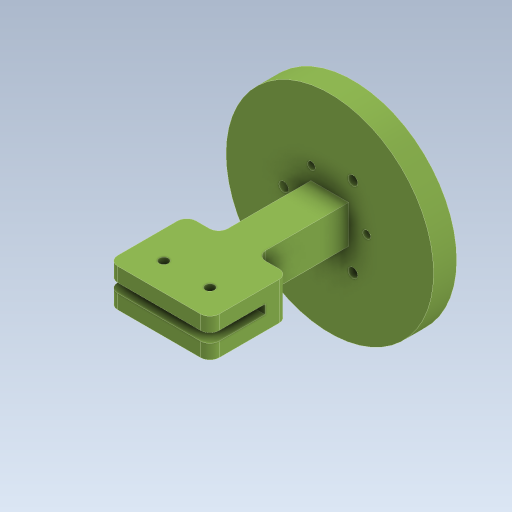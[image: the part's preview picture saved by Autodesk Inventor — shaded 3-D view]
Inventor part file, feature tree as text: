
AUTODESK INVENTOR PART (.ipt)
format: ipt  version: 2023 (Build 270158000, 158)  size: 188,416 bytes
history: native  units: mm
features: extrude x6, sketch x6, mirror x1, fillet x1
ambient origin geometry x8: Origin, YZ Plane, XZ Plane, XY Plane, X Axis, Y Axis, Z Axis, Center Point
bodies: Solid1 (feature_tree)
feature tree (14):
  extrude  "Extrusion1"  Depth=1.7mm
  extrude  "Extrusion2"  Depth=10.0mm
  extrude  "Extrusion3"  Depth=30.0mm TaperAngle=360.0deg
  extrude  "Extrusion4"  Depth=5.0mm TaperAngle=0.0deg
  extrude  "Extrusion5"  Depth=8.2mm
  extrude  "Extrusion6"  Depth=20.0mm TaperAngle=0.0deg
  mirror  "Mirror1"
  fillet  "Fillet1"  Radius=22.0mm
  sketch  "Sketch1"  dims[d0=45.0mm d1=1.7mm]
  sketch  "Sketch2"  dims[d2=2.1mm d3=10.0mm]
  sketch  "Sketch3"  dims[d4=8.0mm d5=30.0mm d7=360.0deg]
  sketch  "Sketch4"  dims[d9=30.0mm d11=360.0deg d13=5.0mm d14=0.0mm]
  sketch  "Sketch5"  dims[d15=8.2mm d16=8.2mm]
  sketch  "Sketch6"  dims[d17=3.0mm d18=0.0mm d19=20.0mm d20=3.0mm d21=0.0mm d22=0.0mm d23=22.0mm d24=8.2mm d25=17.0mm d26=0.0mm d27=2.0mm d28=12.0mm d29=0.0mm d30=6.0mm d31=6.0mm d32=2.0mm d33=0.0mm d34=0.0mm d35=2.0mm d36=0.0mm d37=0.0mm d38=0.0mm]
